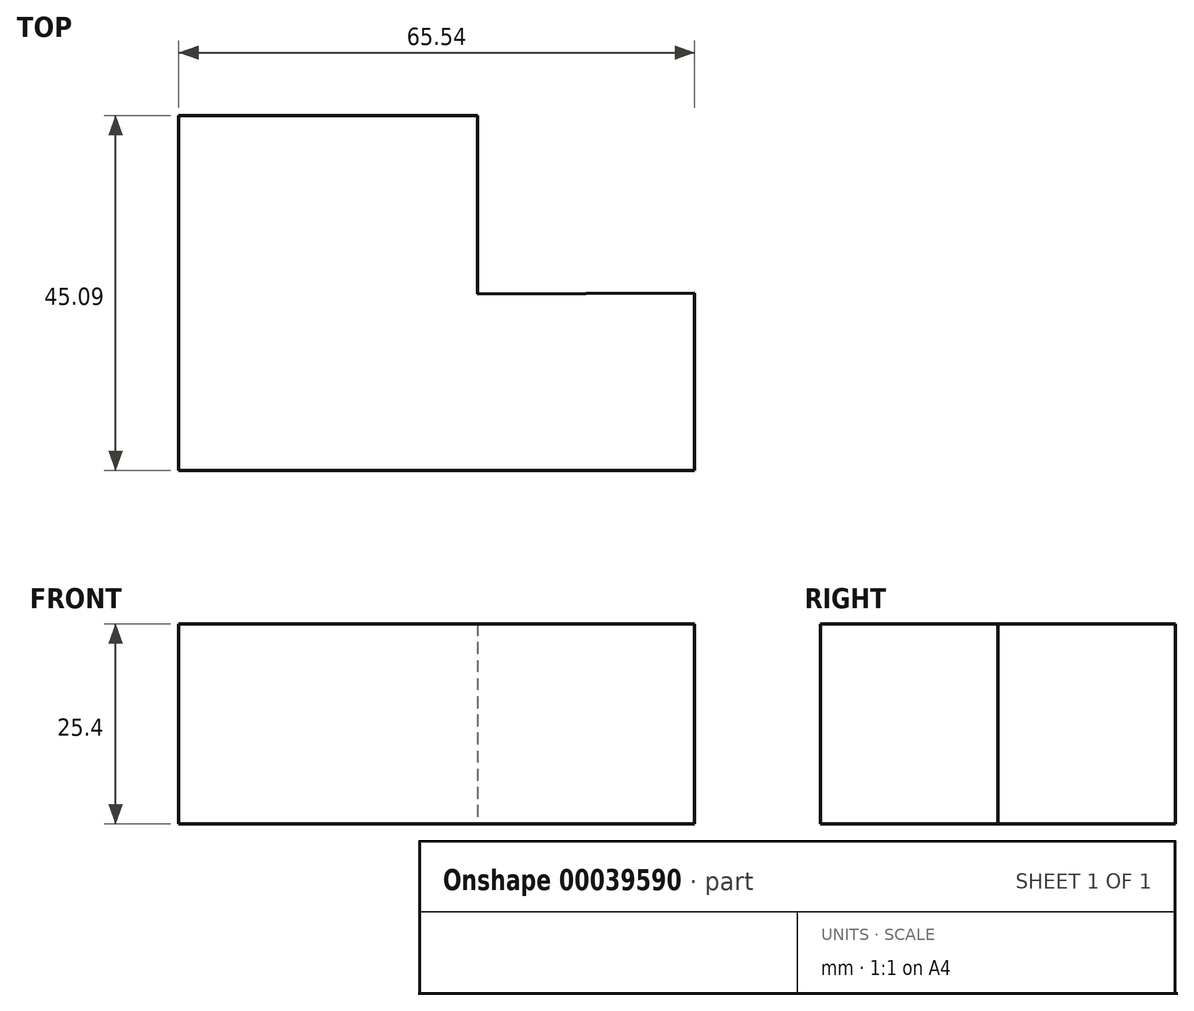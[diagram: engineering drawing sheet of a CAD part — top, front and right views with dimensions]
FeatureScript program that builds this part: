
annotation { "Feature Type Name" : "Feature", "Feature Type Description" : "" }
export const myFeature = defineFeature(function(context is Context, id is Id, definition is map)
    precondition{}
    {
        {
            var Q0;
            Q0=qCreatedBy(makeId("Top.planeOp"),FACE);
            var sketch = newSketch(context, id + "F0", { "sketchPlane" : qUnion([Q0])});
            skLineSegment(sketch, "E0.bottom", {"start": v(0, 0) * mm, "end": v(65.54, 0) * mm});
            skLineSegment(sketch, "E0.top", {"start": v(0, 45.1) * mm, "end": v(37.95, 45.1) * mm});
            skLineSegment(sketch, "E0.left", {"start": v(0, 0) * mm, "end": v(0, 45.1) * mm});
            skLineSegment(sketch, "E0.right", {"start": v(65.54, 0) * mm, "end": v(65.54, 22.55) * mm});
            skLineSegment(sketch, "E1", {"start": v(37.95, 45.1) * mm, "end": v(37.95, 22.42) * mm});
            skLineSegment(sketch, "E2", {"start": v(65.54, 22.55) * mm, "end": v(37.95, 22.42) * mm});
            skPoint(sketch, "E3.orphan", {"position": v(65.54, 45.1) * mm});
            skSolve(sketch);
        }
        {
            var Q0;
            Q0 = qSketchRegion(id + "F0", true);
            extrude(context, id + "F1", {"entities" : qUnion([Q0]), "depth" : 25.4 * mm});
        }
    });
